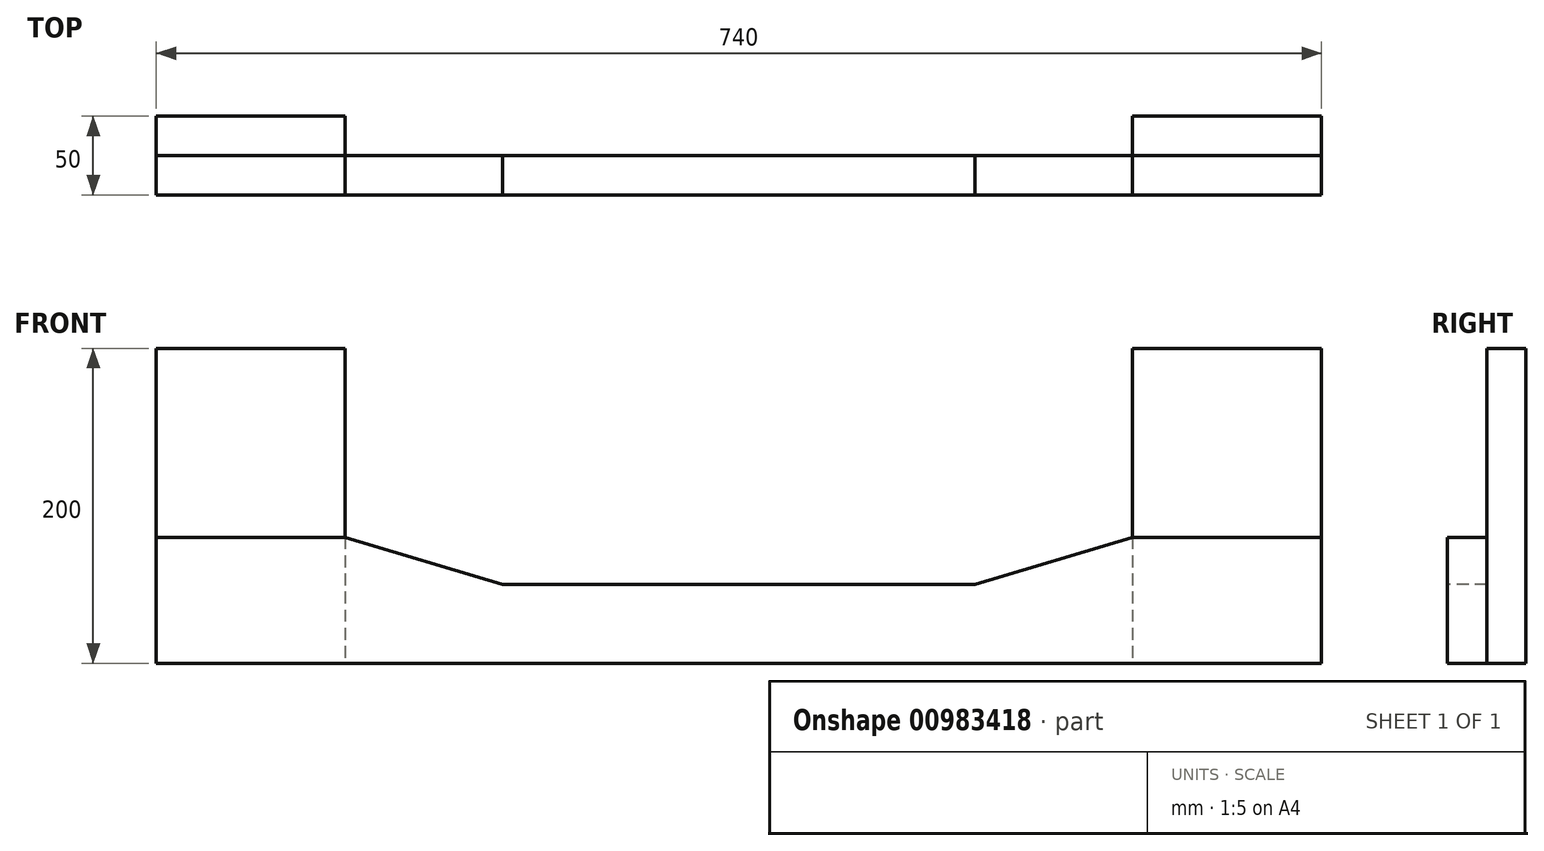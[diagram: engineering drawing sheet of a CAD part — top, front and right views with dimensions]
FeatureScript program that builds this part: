
annotation { "Feature Type Name" : "Feature", "Feature Type Description" : "" }
export const myFeature = defineFeature(function(context is Context, id is Id, definition is map)
    precondition{}
    {
        {
            var Q0;
            Q0=qCreatedBy(makeId("Front.planeOp"),FACE);
            var sketch = newSketch(context, id + "F0", { "sketchPlane" : qUnion([Q0])});
            skLineSegment(sketch, "E0.bottom", {"start": v(-370, 120) * mm, "end": v(-250, 120) * mm});
            skLineSegment(sketch, "E0.top", {"start": v(-370, -80) * mm, "end": v(-250, -80) * mm});
            skLineSegment(sketch, "E0.left", {"start": v(-370, 120) * mm, "end": v(-370, -80) * mm});
            skLineSegment(sketch, "E0.right", {"start": v(-250, 120) * mm, "end": v(-250, -80) * mm});
            skSolve(sketch);
        }
        {
            var Q0;
            Q0 = qSketchRegion(id + "F0", true);
            extrude(context, id + "F1", {"entities" : qUnion([Q0]), "depth" : 25 * mm, "offsetDistance" : 25 * mm});
        }
        {
            var Q0;
            Q0=makeQuery(id+"F1.opExtrude","SWEPT_BODY",BODY,{"disambiguationData":[OSD([sQuery(id+"F0.wireOp",EDGE,"E0.bottom"),sQuery(id+"F0.wireOp",EDGE,"E0.top"),sQuery(id+"F0.wireOp",EDGE,"E0.left"),sQuery(id+"F0.wireOp",EDGE,"E0.right")])]});
            var Q1;
            Q1=qCreatedBy(makeId("Right.planeOp"),FACE);
            mirror(context, id + "F2", {"entities" : qUnion([Q0]), "mirrorPlane" : qUnion([Q1])});
        }
        {
            var Q0;
            Q0=makeQuery(id+"F1.opExtrude","CAP_FACE",FACE,{"disambiguationData":[OSD([sQuery(id+"F0.wireOp",EDGE,"E0.bottom"),sQuery(id+"F0.wireOp",EDGE,"E0.top"),sQuery(id+"F0.wireOp",EDGE,"E0.left"),sQuery(id+"F0.wireOp",EDGE,"E0.right")])],"isStart":false});
            var sketch = newSketch(context, id + "F3", { "sketchPlane" : qUnion([Q0])});
            skLineSegment(sketch, "E1.0", {"start": v(-370, 120) * mm, "end": v(-370, -80) * mm, "construction": true});
            skLineSegment(sketch, "E2.0", {"start": v(370, 120) * mm, "end": v(370, -80) * mm, "construction": true});
            skLineSegment(sketch, "E3.bottom", {"start": v(-370, -80) * mm, "end": v(370, -80) * mm});
            skLineSegment(sketch, "E3.top", {"start": v(-370, 0) * mm, "end": v(370, 0) * mm});
            skLineSegment(sketch, "E3.left", {"start": v(-370, -80) * mm, "end": v(-370, 0) * mm});
            skLineSegment(sketch, "E3.right", {"start": v(370, -80) * mm, "end": v(370, 0) * mm});
            skSolve(sketch);
        }
        {
            var Q0;
            Q0 = qSketchRegion(id + "F3", true);
            extrude(context, id + "F4", {"entities" : qUnion([Q0]), "depth" : 25 * mm, "offsetDistance" : 25 * mm});
        }
        {
            var Q0;
            Q0=makeQuery(id+"F4.opExtrude","CAP_FACE",FACE,{"disambiguationData":[OSD([sQuery(id+"F3.wireOp",EDGE,"E3.bottom"),sQuery(id+"F3.wireOp",EDGE,"E3.top"),sQuery(id+"F3.wireOp",EDGE,"E3.left"),sQuery(id+"F3.wireOp",EDGE,"E3.right")])],"isStart":false});
            var sketch = newSketch(context, id + "F5", { "sketchPlane" : qUnion([Q0])});
            skLineSegment(sketch, "E4.0", {"start": v(-370, 0) * mm, "end": v(370, 0) * mm, "construction": true});
            skLineSegment(sketch, "E5.0", {"start": v(-370, -80) * mm, "end": v(370, -80) * mm, "construction": true});
            skLineSegment(sketch, "E6", {"start": v(0, 0) * mm, "end": v(0, -80) * mm, "construction": true});
            skLineSegment(sketch, "E7.0", {"start": v(-250, 120) * mm, "end": v(-250, -80) * mm, "construction": true});
            skLineSegment(sketch, "E8", {"start": v(-250, 0) * mm, "end": v(-150, -30) * mm});
            skLineSegment(sketch, "E9", {"start": v(-150, -30) * mm, "end": v(0, -30) * mm});
            skLineSegment(sketch, "E10", {"start": v(-250, 0) * mm, "end": v(0, 0) * mm});
            skLineSegment(sketch, "E11.MirrorCS", {"start": v(150, -30) * mm, "end": v(0, -30) * mm});
            skLineSegment(sketch, "E12.MirrorCS", {"start": v(250, 0) * mm, "end": v(150, -30) * mm});
            skLineSegment(sketch, "E13.MirrorCS", {"start": v(250, 0) * mm, "end": v(0, 0) * mm});
            skSolve(sketch);
        }
        {
            var Q0;
            Q0 = qSketchRegion(id + "F5", true);
            extrude(context, id + "F6", {"entities" : qUnion([Q0]), "operationType" : NewBodyOperationType.REMOVE, "endBound" : BoundingType.THROUGH_ALL, "oppositeDirection" : true, "depth" : 25 * mm, "offsetDistance" : 25 * mm});
        }
    });
